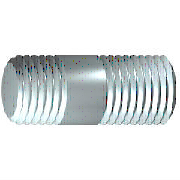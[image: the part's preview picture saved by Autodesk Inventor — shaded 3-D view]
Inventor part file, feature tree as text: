
AUTODESK INVENTOR PART (.ipt)
format: ipt  version: 2017 (Build 210142000, 142)  size: 148,480 bytes
history: native  units: mm (DEFAULTED — no unit token found)
features: sketch x1
ambient origin geometry x8: Origin, YZ Plane, XZ Plane, XY Plane, X Axis, Y Axis, Z Axis, Center Point
bodies: Solid1 (feature_tree), Body (feature_tree)
feature tree (1):
  sketch  "Sketch1"  dims[d0=3.0mm d3=90.0deg d1=3.0mm d2=0.0mm d4=3.0mm d5=14.0mm d6=12.0mm d7=12.306725mm d8=0.0mm d9=0.307725mm d10=0.306725mm d11=0.501mm d12=0.306725mm d13=3.0mm d69=45.0deg d70=45.0deg d78=0.0mm d80=-12.306725mm d86=-2.5mm]
